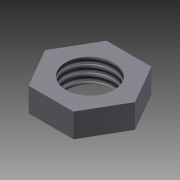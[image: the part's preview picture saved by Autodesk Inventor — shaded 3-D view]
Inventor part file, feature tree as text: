
AUTODESK INVENTOR PART (.ipt)
format: ipt  version: 2012 (Build 160160000, 160)  size: 82,944 bytes
history: native  units: mm
features: extrude x1, thread x1, sketch x1
ambient origin geometry x8: Origin, YZ Plane, XZ Plane, XY Plane, X Axis, Y Axis, Z Axis, Center Point
bodies: Solid1 (feature_tree)
feature tree (3):
  extrude  "Extrusion1"  Depth=13.0mm
  thread  "Thread1"  [1 undecoded]
  sketch  "Sketch1"  dims[d0=8.0mm d2=13.0mm d3=4.0mm d4=0.0mm d5=10.0mm d6=0.0mm]
note: 1 required parameter value undecoded (feature->parameter linkage not recoverable at this tier; creation-order binding heuristic only, values carry confidence <= 0.55)
